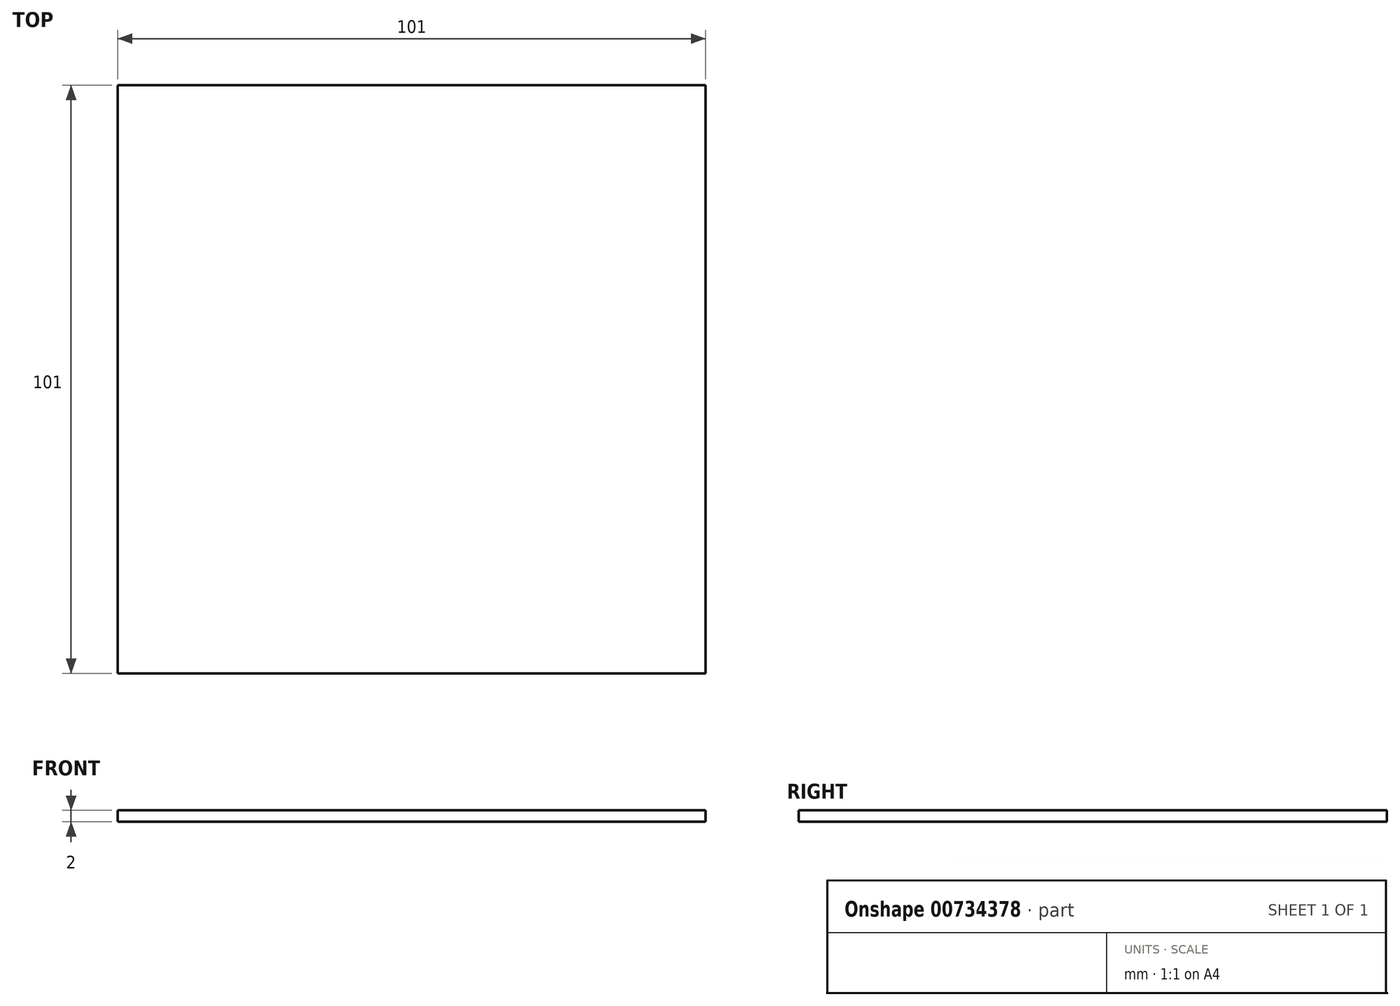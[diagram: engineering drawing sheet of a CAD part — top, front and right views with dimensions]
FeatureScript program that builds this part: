
annotation { "Feature Type Name" : "Feature", "Feature Type Description" : "" }
export const myFeature = defineFeature(function(context is Context, id is Id, definition is map)
    precondition{}
    {
        {
            var Q0;
            Q0=qCreatedBy(makeId("Top.planeOp"),FACE);
            var sketch = newSketch(context, id + "F0", { "sketchPlane" : qUnion([Q0])});
            skLineSegment(sketch, "E0.bottom", {"start": v(-55.74, 49.08) * mm, "end": v(45.26, 49.08) * mm});
            skLineSegment(sketch, "E0.top", {"start": v(-55.74, -51.92) * mm, "end": v(45.26, -51.92) * mm});
            skLineSegment(sketch, "E0.left", {"start": v(-55.74, 49.08) * mm, "end": v(-55.74, -51.92) * mm});
            skLineSegment(sketch, "E0.right", {"start": v(45.26, 49.08) * mm, "end": v(45.26, -51.92) * mm});
            skSolve(sketch);
        }
        {
            var Q0;
            Q0 = qSketchRegion(id + "F0", true);
            extrude(context, id + "F1", {"entities" : qUnion([Q0]), "depth" : 2 * mm, "offsetDistance" : 25 * mm});
        }
    });
